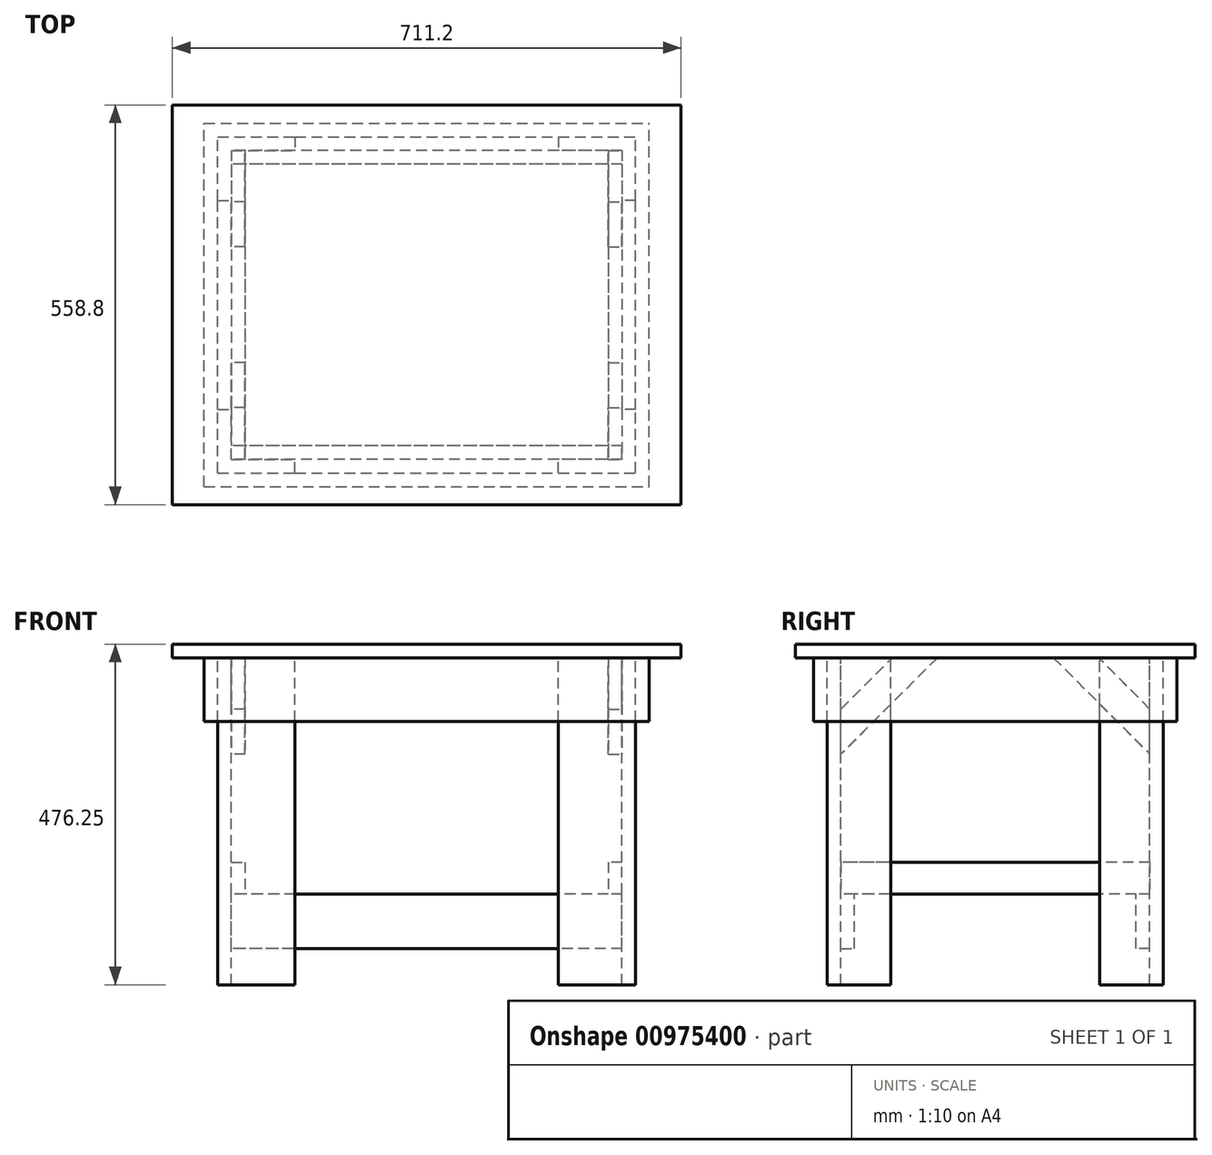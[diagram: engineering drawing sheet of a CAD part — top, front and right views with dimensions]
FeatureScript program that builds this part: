
annotation { "Feature Type Name" : "Feature", "Feature Type Description" : "" }
export const myFeature = defineFeature(function(context is Context, id is Id, definition is map)
    precondition{}
    {
        {
            var Q0;
            Q0=qCreatedBy(makeId("Top.planeOp"),FACE);
            var sketch = newSketch(context, id + "F0", { "sketchPlane" : qUnion([Q0])});
            skLineSegment(sketch, "E0.bottom", {"start": v(355.6, 279.4) * mm, "end": v(-355.6, 279.4) * mm});
            skLineSegment(sketch, "E0.top", {"start": v(355.6, -279.4) * mm, "end": v(-355.6, -279.4) * mm});
            skLineSegment(sketch, "E0.left", {"start": v(355.6, 279.4) * mm, "end": v(355.6, -279.4) * mm});
            skLineSegment(sketch, "E0.right", {"start": v(-355.6, 279.4) * mm, "end": v(-355.6, -279.4) * mm});
            skPoint(sketch, "E0.middle", {"position": v(0, 0) * mm});
            skSolve(sketch);
        }
        {
            var Q0;
            Q0=makeQuery(id+"F0.imprint","IMPRINT",FACE,{"disambiguationData":[TD([[makeQuery(id+"F0.imprint","IMPRINT",EDGE,{"derivedFrom":sQuery(id+"F0.wireOp",EDGE,"E0.bottom")}),1.0]])]});
            extrude(context, id + "F1", {"entities" : qUnion([Q0]), "oppositeDirection" : true, "depth" : 19.05 * mm, "offsetDistance" : 25.4 * mm});
        }
        {
            var Q0;
            Q0=makeQuery(id+"F1.opExtrude","CAP_FACE",FACE,{"disambiguationData":[OSD([sQuery(id+"F0.wireOp",EDGE,"E0.bottom"),sQuery(id+"F0.wireOp",EDGE,"E0.top"),sQuery(id+"F0.wireOp",EDGE,"E0.left"),sQuery(id+"F0.wireOp",EDGE,"E0.right")])],"isStart":false});
            var sketch = newSketch(context, id + "F2", { "sketchPlane" : qUnion([Q0])});
            skLineSegment(sketch, "E1.bottom", {"start": v(-311.15, 254) * mm, "end": v(311.15, 254) * mm});
            skLineSegment(sketch, "E1.top", {"start": v(-311.15, 234.95) * mm, "end": v(311.15, 234.95) * mm});
            skLineSegment(sketch, "E1.left", {"start": v(-311.15, 254) * mm, "end": v(-311.15, 234.95) * mm});
            skLineSegment(sketch, "E1.right", {"start": v(311.15, 254) * mm, "end": v(311.15, 234.95) * mm});
            skLineSegment(sketch, "E2.MirrorCS", {"start": v(-311.15, -254) * mm, "end": v(311.15, -254) * mm});
            skLineSegment(sketch, "E3.MirrorCS", {"start": v(-311.15, -234.95) * mm, "end": v(311.15, -234.95) * mm});
            skLineSegment(sketch, "E4.MirrorCS", {"start": v(-311.15, -254) * mm, "end": v(-311.15, -234.95) * mm});
            skLineSegment(sketch, "E5.MirrorCS", {"start": v(311.15, -254) * mm, "end": v(311.15, -234.95) * mm});
            skSolve(sketch);
        }
        {
            var Q0;
            Q0 = qSketchRegion(id + "F2", true);
            extrude(context, id + "F3", {"entities" : qUnion([Q0]), "operationType" : NewBodyOperationType.ADD, "depth" : 88.9 * mm, "offsetDistance" : 25.4 * mm});
        }
        {
            var Q0;
            Q0=makeQuery(id+"F1.opExtrude","CAP_FACE",FACE,{"disambiguationData":[OSD([sQuery(id+"F0.wireOp",EDGE,"E0.bottom"),sQuery(id+"F0.wireOp",EDGE,"E0.top"),sQuery(id+"F0.wireOp",EDGE,"E0.left"),sQuery(id+"F0.wireOp",EDGE,"E0.right")])],"isStart":false});
            var sketch = newSketch(context, id + "F4", { "sketchPlane" : qUnion([Q0])});
            skLineSegment(sketch, "E6.bottom", {"start": v(-311.15, 234.95) * mm, "end": v(-292.1, 234.95) * mm});
            skLineSegment(sketch, "E6.top", {"start": v(-311.15, -234.95) * mm, "end": v(-292.1, -234.95) * mm});
            skLineSegment(sketch, "E6.left", {"start": v(-311.15, 234.95) * mm, "end": v(-311.15, -234.95) * mm});
            skLineSegment(sketch, "E6.right", {"start": v(-292.1, 234.95) * mm, "end": v(-292.1, -234.95) * mm});
            skLineSegment(sketch, "E7.MirrorCS", {"start": v(311.15, 234.95) * mm, "end": v(292.1, 234.95) * mm});
            skLineSegment(sketch, "E8.MirrorCS", {"start": v(311.15, 234.95) * mm, "end": v(311.15, -234.95) * mm});
            skLineSegment(sketch, "E9.MirrorCS", {"start": v(292.1, 234.95) * mm, "end": v(292.1, -234.95) * mm});
            skLineSegment(sketch, "E10.MirrorCS", {"start": v(311.15, -234.95) * mm, "end": v(292.1, -234.95) * mm});
            skSolve(sketch);
        }
        {
            var Q0;
            Q0 = qSketchRegion(id + "F4", true);
            extrude(context, id + "F5", {"entities" : qUnion([Q0]), "operationType" : NewBodyOperationType.ADD, "depth" : 88.9 * mm, "offsetDistance" : 25.4 * mm});
        }
        {
            var Q0;
            {var subQ0=sQuery(id+"F4.wireOp",EDGE,"E6.right");Q0=makeQuery(id+"F4.imprint","IMPRINT",FACE,{"disambiguationData":[TD([[makeQuery(id+"F4.imprint","IMPRINT",EDGE,{"derivedFrom":subQ0}),1.0]])]});}
            var sketch = newSketch(context, id + "F6", { "sketchPlane" : qUnion([Q0])});
            skLineSegment(sketch, "E11.bottom", {"start": v(-292.1, 234.95) * mm, "end": v(292.1, 234.95) * mm, "construction": true});
            skLineSegment(sketch, "E11.right", {"start": v(292.1, 234.95) * mm, "end": v(292.1, -234.95) * mm, "construction": true});
            skLineSegment(sketch, "E12.bottom", {"start": v(-292.1, 234.95) * mm, "end": v(-273.05, 234.95) * mm});
            skLineSegment(sketch, "E12.top", {"start": v(-292.1, 146.05) * mm, "end": v(-273.05, 146.05) * mm});
            skLineSegment(sketch, "E12.right", {"start": v(-273.05, 234.95) * mm, "end": v(-273.05, 146.05) * mm});
            skLineSegment(sketch, "E13.bottom", {"start": v(-273.05, 234.95) * mm, "end": v(-184.15, 234.95) * mm});
            skLineSegment(sketch, "E13.top", {"start": v(-273.05, 215.9) * mm, "end": v(-184.15, 215.9) * mm});
            skLineSegment(sketch, "E13.left", {"start": v(-273.05, 234.95) * mm, "end": v(-273.05, 215.9) * mm});
            skLineSegment(sketch, "E13.right", {"start": v(-184.15, 234.95) * mm, "end": v(-184.15, 215.9) * mm});
            skLineSegment(sketch, "E14.MirrorCS", {"start": v(292.1, 234.95) * mm, "end": v(292.1, 184.15) * mm});
            skLineSegment(sketch, "E15", {"start": v(-292.1, 234.95) * mm, "end": v(-292.1, 146.05) * mm});
            skLineSegment(sketch, "E16.MirrorCS", {"start": v(292.1, 234.95) * mm, "end": v(273.05, 234.95) * mm});
            skLineSegment(sketch, "E17.MirrorCS", {"start": v(292.1, 146.05) * mm, "end": v(273.05, 146.05) * mm});
            skLineSegment(sketch, "E18.MirrorCS", {"start": v(184.15, 234.95) * mm, "end": v(184.15, 215.9) * mm});
            skLineSegment(sketch, "E19.MirrorCS", {"start": v(273.05, 234.95) * mm, "end": v(273.05, 215.9) * mm});
            skLineSegment(sketch, "E20.MirrorCS", {"start": v(273.05, 215.9) * mm, "end": v(184.15, 215.9) * mm});
            skLineSegment(sketch, "E21.MirrorCS", {"start": v(273.05, 234.95) * mm, "end": v(273.05, 146.05) * mm});
            skLineSegment(sketch, "E22.MirrorCS", {"start": v(292.1, 234.95) * mm, "end": v(292.1, 146.05) * mm});
            skLineSegment(sketch, "E23.MirrorCS", {"start": v(273.05, 234.95) * mm, "end": v(184.15, 234.95) * mm});
            skLineSegment(sketch, "E24.MirrorCS", {"start": v(292.1, -234.95) * mm, "end": v(273.05, -234.95) * mm});
            skLineSegment(sketch, "E25.MirrorCS", {"start": v(-292.1, -234.95) * mm, "end": v(-273.05, -234.95) * mm});
            skLineSegment(sketch, "E26.MirrorCS", {"start": v(292.1, -234.95) * mm, "end": v(292.1, -184.15) * mm});
            skLineSegment(sketch, "E27.MirrorCS", {"start": v(-273.05, -234.95) * mm, "end": v(-273.05, -215.9) * mm});
            skLineSegment(sketch, "E28.MirrorCS", {"start": v(-184.15, -234.95) * mm, "end": v(-184.15, -215.9) * mm});
            skLineSegment(sketch, "E29.MirrorCS", {"start": v(-292.1, -146.05) * mm, "end": v(-273.05, -146.05) * mm});
            skLineSegment(sketch, "E30.MirrorCS", {"start": v(184.15, -234.95) * mm, "end": v(184.15, -215.9) * mm});
            skLineSegment(sketch, "E31.MirrorCS", {"start": v(292.1, -146.05) * mm, "end": v(273.05, -146.05) * mm});
            skLineSegment(sketch, "E32.MirrorCS", {"start": v(273.05, -234.95) * mm, "end": v(273.05, -215.9) * mm});
            skLineSegment(sketch, "E33.MirrorCS", {"start": v(-273.05, -234.95) * mm, "end": v(-184.15, -234.95) * mm});
            skLineSegment(sketch, "E34.MirrorCS", {"start": v(273.05, -234.95) * mm, "end": v(184.15, -234.95) * mm});
            skLineSegment(sketch, "E35.MirrorCS", {"start": v(-292.1, -234.95) * mm, "end": v(292.1, -234.95) * mm, "construction": true});
            skLineSegment(sketch, "E36.MirrorCS", {"start": v(-292.1, -234.95) * mm, "end": v(-292.1, -146.05) * mm});
            skLineSegment(sketch, "E37.MirrorCS", {"start": v(-273.05, -215.9) * mm, "end": v(-184.15, -215.9) * mm});
            skLineSegment(sketch, "E38.MirrorCS", {"start": v(-273.05, -234.95) * mm, "end": v(-273.05, -146.05) * mm});
            skLineSegment(sketch, "E39.MirrorCS", {"start": v(292.1, -234.95) * mm, "end": v(292.1, -146.05) * mm});
            skLineSegment(sketch, "E40.MirrorCS", {"start": v(273.05, -234.95) * mm, "end": v(273.05, -146.05) * mm});
            skLineSegment(sketch, "E41.MirrorCS", {"start": v(273.05, -215.9) * mm, "end": v(184.15, -215.9) * mm});
            skSolve(sketch);
        }
        {
            var Q0;
            Q0 = qSketchRegion(id + "F6", true);
            extrude(context, id + "F7", {"entities" : qUnion([Q0]), "operationType" : NewBodyOperationType.ADD, "depth" : 457.2 * mm, "offsetDistance" : 25.4 * mm});
        }
        {
            var Q0;
            Q0=makeQuery(id+"F7.opExtrude","CAP_FACE",FACE,{"disambiguationData":[OSD([sQuery(id+"F6.wireOp",EDGE,"00a5e765-ee14-44ce-a59f-6ea5d8c154d11.MirrorCS"),sQuery(id+"F6.wireOp",EDGE,"00a5e765-ee14-44ce-a59f-6ea5d8c154d16.MirrorCS"),sQuery(id+"F6.wireOp",EDGE,"00a5e765-ee14-44ce-a59f-6ea5d8c154d19.MirrorCS"),sQuery(id+"F6.wireOp",EDGE,"00a5e765-ee14-44ce-a59f-6ea5d8c154d114.MirrorCS"),sQuery(id+"F6.wireOp",EDGE,"00a5e765-ee14-44ce-a59f-6ea5d8c154d118.MirrorCS"),sQuery(id+"F6.wireOp",EDGE,"00a5e765-ee14-44ce-a59f-6ea5d8c154d119.MirrorCS"),sQuery(id+"F6.wireOp",EDGE,"00a5e765-ee14-44ce-a59f-6ea5d8c154d121.MirrorCS")])],"isStart":false});
            var Q1;
            Q1=makeQuery(id+"F5.boolean.opBoolean","SPLIT",FACE,{"disambiguationData":[TD([makeQuery(id+"F3.opExtrude","SWEPT_FACE",FACE,{"disambiguationData":[OSD([sQuery(id+"F2.wireOp",EDGE,"E1.top")])]})])],"derivedFrom":makeQuery(id+"F1.opExtrude","CAP_FACE",FACE,{"disambiguationData":[OSD([sQuery(id+"F0.wireOp",EDGE,"E0.bottom"),sQuery(id+"F0.wireOp",EDGE,"E0.top"),sQuery(id+"F0.wireOp",EDGE,"E0.left"),sQuery(id+"F0.wireOp",EDGE,"E0.right")])],"isStart":false})});
            cPlane(context, id + "F8", {"entities" : qUnion([Q0, Q1]), "cplaneType" : CPlaneType.OFFSET, "offset" : 330.2 * mm, "width" : 152.4 * mm, "height" : 152.4 * mm});
        }
        {
            var Q0;
            Q0=qCreatedBy(id+"F8.planeOp",FACE);
            var sketch = newSketch(context, id + "F9", { "sketchPlane" : qUnion([Q0])});
            skLineSegment(sketch, "E42.bottom", {"start": v(273.05, -215.9) * mm, "end": v(-273.05, -215.9) * mm});
            skLineSegment(sketch, "E42.top", {"start": v(273.05, -196.85) * mm, "end": v(-273.05, -196.85) * mm});
            skLineSegment(sketch, "E42.left", {"start": v(273.05, -215.9) * mm, "end": v(273.05, -196.85) * mm});
            skLineSegment(sketch, "E42.right", {"start": v(-273.05, -215.9) * mm, "end": v(-273.05, -196.85) * mm});
            skLineSegment(sketch, "E43", {"start": v(0, 0) * mm, "end": v(0, -196.85) * mm, "construction": true});
            skLineSegment(sketch, "E44.MirrorCS", {"start": v(273.05, 196.85) * mm, "end": v(-273.05, 196.85) * mm});
            skLineSegment(sketch, "E45.MirrorCS", {"start": v(273.05, 215.9) * mm, "end": v(-273.05, 215.9) * mm});
            skLineSegment(sketch, "E46.MirrorCS", {"start": v(-273.05, 215.9) * mm, "end": v(-273.05, 196.85) * mm});
            skLineSegment(sketch, "E47.MirrorCS", {"start": v(273.05, 215.9) * mm, "end": v(273.05, 196.85) * mm});
            skSolve(sketch);
        }
        {
            var Q0;
            Q0 = qSketchRegion(id + "F9", true);
            extrude(context, id + "F10", {"entities" : qUnion([Q0]), "operationType" : NewBodyOperationType.ADD, "depth" : 76.2 * mm, "offsetDistance" : 25.4 * mm});
        }
        {
            var Q0;
            Q0=qCreatedBy(id+"F8.planeOp",FACE);
            var sketch = newSketch(context, id + "F11", { "sketchPlane" : qUnion([Q0])});
            skLineSegment(sketch, "E48.bottom", {"start": v(273.05, -215.9) * mm, "end": v(254, -215.9) * mm});
            skLineSegment(sketch, "E48.top", {"start": v(273.05, 215.9) * mm, "end": v(254, 215.9) * mm});
            skLineSegment(sketch, "E48.left", {"start": v(273.05, -215.9) * mm, "end": v(273.05, 215.9) * mm});
            skLineSegment(sketch, "E48.right", {"start": v(254, -215.9) * mm, "end": v(254, 215.9) * mm});
            skLineSegment(sketch, "E49", {"start": v(0, 0) * mm, "end": v(254, 0) * mm});
            skLineSegment(sketch, "E50.MirrorCS", {"start": v(-254, -215.9) * mm, "end": v(-254, 215.9) * mm});
            skLineSegment(sketch, "E51.MirrorCS", {"start": v(-273.05, -215.9) * mm, "end": v(-254, -215.9) * mm});
            skLineSegment(sketch, "E52.MirrorCS", {"start": v(-273.05, -215.9) * mm, "end": v(-273.05, 215.9) * mm});
            skLineSegment(sketch, "E53.MirrorCS", {"start": v(-273.05, 215.9) * mm, "end": v(-254, 215.9) * mm});
            skSolve(sketch);
        }
        {
            var Q0;
            Q0 = qSketchRegion(id + "F11", true);
            extrude(context, id + "F12", {"entities" : qUnion([Q0]), "operationType" : NewBodyOperationType.ADD, "oppositeDirection" : true, "depth" : 44.45 * mm, "offsetDistance" : 25.4 * mm});
        }
        {
            var Q0;
            Q0=makeQuery(id+"F12.boolean.opBoolean","SPLIT",FACE,{"disambiguationData":[TD([makeQuery(id+"F1.opExtrude","CAP_FACE",FACE,{"disambiguationData":[OSD([sQuery(id+"F0.wireOp",EDGE,"E0.bottom"),sQuery(id+"F0.wireOp",EDGE,"E0.top"),sQuery(id+"F0.wireOp",EDGE,"E0.left"),sQuery(id+"F0.wireOp",EDGE,"E0.right")])],"isStart":false})])],"derivedFrom":makeQuery(id+"F7.opExtrude","SWEPT_FACE",FACE,{"disambiguationData":[OSD([sQuery(id+"F6.wireOp",EDGE,"E21.MirrorCS")])]})});
            var sketch = newSketch(context, id + "F13", { "sketchPlane" : qUnion([Q0])});
            skLineSegment(sketch, "E54", {"start": v(-324.44, 0) * mm, "end": v(352.42, 0) * mm, "construction": true});
            skLineSegment(sketch, "E55", {"start": v(-215.9, 80.43) * mm, "end": v(-215.9, -380.2) * mm, "construction": true});
            skLineSegment(sketch, "E56.MirrorCS", {"start": v(215.9, 80.43) * mm, "end": v(215.9, -380.2) * mm, "construction": true});
            skLineSegment(sketch, "E57", {"start": v(-327.65, -19.05) * mm, "end": v(355.1, -19.05) * mm, "construction": true});
            skLineSegment(sketch, "E58", {"start": v(-215.9, -90.9) * mm, "end": v(-144.06, -19.05) * mm});
            skLineSegment(sketch, "E59", {"start": v(-144.06, -19.05) * mm, "end": v(-81.2, -19.05) * mm});
            skLineSegment(sketch, "E60", {"start": v(-81.2, -19.05) * mm, "end": v(-215.9, -153.75) * mm});
            skLineSegment(sketch, "E61", {"start": v(-215.9, -153.75) * mm, "end": v(-215.9, -90.9) * mm});
            skLineSegment(sketch, "E62.MirrorCS", {"start": v(215.9, -90.9) * mm, "end": v(144.06, -19.05) * mm});
            skLineSegment(sketch, "E63.MirrorCS", {"start": v(81.2, -19.05) * mm, "end": v(215.9, -153.75) * mm});
            skLineSegment(sketch, "E64", {"start": v(81.2, -19.05) * mm, "end": v(144.06, -19.05) * mm});
            skLineSegment(sketch, "E65", {"start": v(215.9, -90.9) * mm, "end": v(215.9, -153.75) * mm});
            skSolve(sketch);
        }
        {
            var Q0;
            Q0 = qSketchRegion(id + "F13", true);
            extrude(context, id + "F14", {"entities" : qUnion([Q0]), "operationType" : NewBodyOperationType.ADD, "depth" : 19.05 * mm, "offsetDistance" : 25.4 * mm});
        }
        {
            var Q0;
            Q0=makeQuery(id+"F12.boolean.opBoolean","SPLIT",FACE,{"disambiguationData":[TD([makeQuery(id+"F1.opExtrude","CAP_FACE",FACE,{"disambiguationData":[OSD([sQuery(id+"F0.wireOp",EDGE,"E0.bottom"),sQuery(id+"F0.wireOp",EDGE,"E0.top"),sQuery(id+"F0.wireOp",EDGE,"E0.left"),sQuery(id+"F0.wireOp",EDGE,"E0.right")])],"isStart":false})])],"derivedFrom":makeQuery(id+"F7.opExtrude","SWEPT_FACE",FACE,{"disambiguationData":[OSD([sQuery(id+"F6.wireOp",EDGE,"E38.MirrorCS")])]})});
            var sketch = newSketch(context, id + "F15", { "sketchPlane" : qUnion([Q0])});
            skLineSegment(sketch, "E66", {"start": v(-293.81, 0) * mm, "end": v(295.71, 0) * mm, "construction": true});
            skLineSegment(sketch, "E67", {"start": v(-293.81, -19.05) * mm, "end": v(295.71, -19.05) * mm, "construction": true});
            skLineSegment(sketch, "E68", {"start": v(-215.9, 72.85) * mm, "end": v(-215.9, -185.14) * mm, "construction": true});
            skLineSegment(sketch, "E69.MirrorCS", {"start": v(215.9, 72.85) * mm, "end": v(215.9, -185.14) * mm, "construction": true});
            skLineSegment(sketch, "E70", {"start": v(-215.9, -90.9) * mm, "end": v(-144.06, -19.05) * mm});
            skLineSegment(sketch, "E71", {"start": v(-144.06, -19.05) * mm, "end": v(-81.2, -19.05) * mm});
            skLineSegment(sketch, "E72", {"start": v(-81.2, -19.05) * mm, "end": v(-215.9, -153.75) * mm});
            skLineSegment(sketch, "E73", {"start": v(-215.9, -153.75) * mm, "end": v(-215.9, -90.9) * mm});
            skLineSegment(sketch, "E74.MirrorCS", {"start": v(81.2, -19.05) * mm, "end": v(215.9, -153.75) * mm});
            skLineSegment(sketch, "E75.MirrorCS", {"start": v(215.9, -90.9) * mm, "end": v(144.06, -19.05) * mm});
            skLineSegment(sketch, "E76", {"start": v(81.2, -19.05) * mm, "end": v(144.06, -19.05) * mm});
            skLineSegment(sketch, "E77", {"start": v(215.9, -90.9) * mm, "end": v(215.9, -153.75) * mm});
            skSolve(sketch);
        }
        {
            var Q0;
            Q0 = qSketchRegion(id + "F15", true);
            extrude(context, id + "F16", {"entities" : qUnion([Q0]), "operationType" : NewBodyOperationType.ADD, "depth" : 19.05 * mm, "offsetDistance" : 25.4 * mm});
        }
    });
